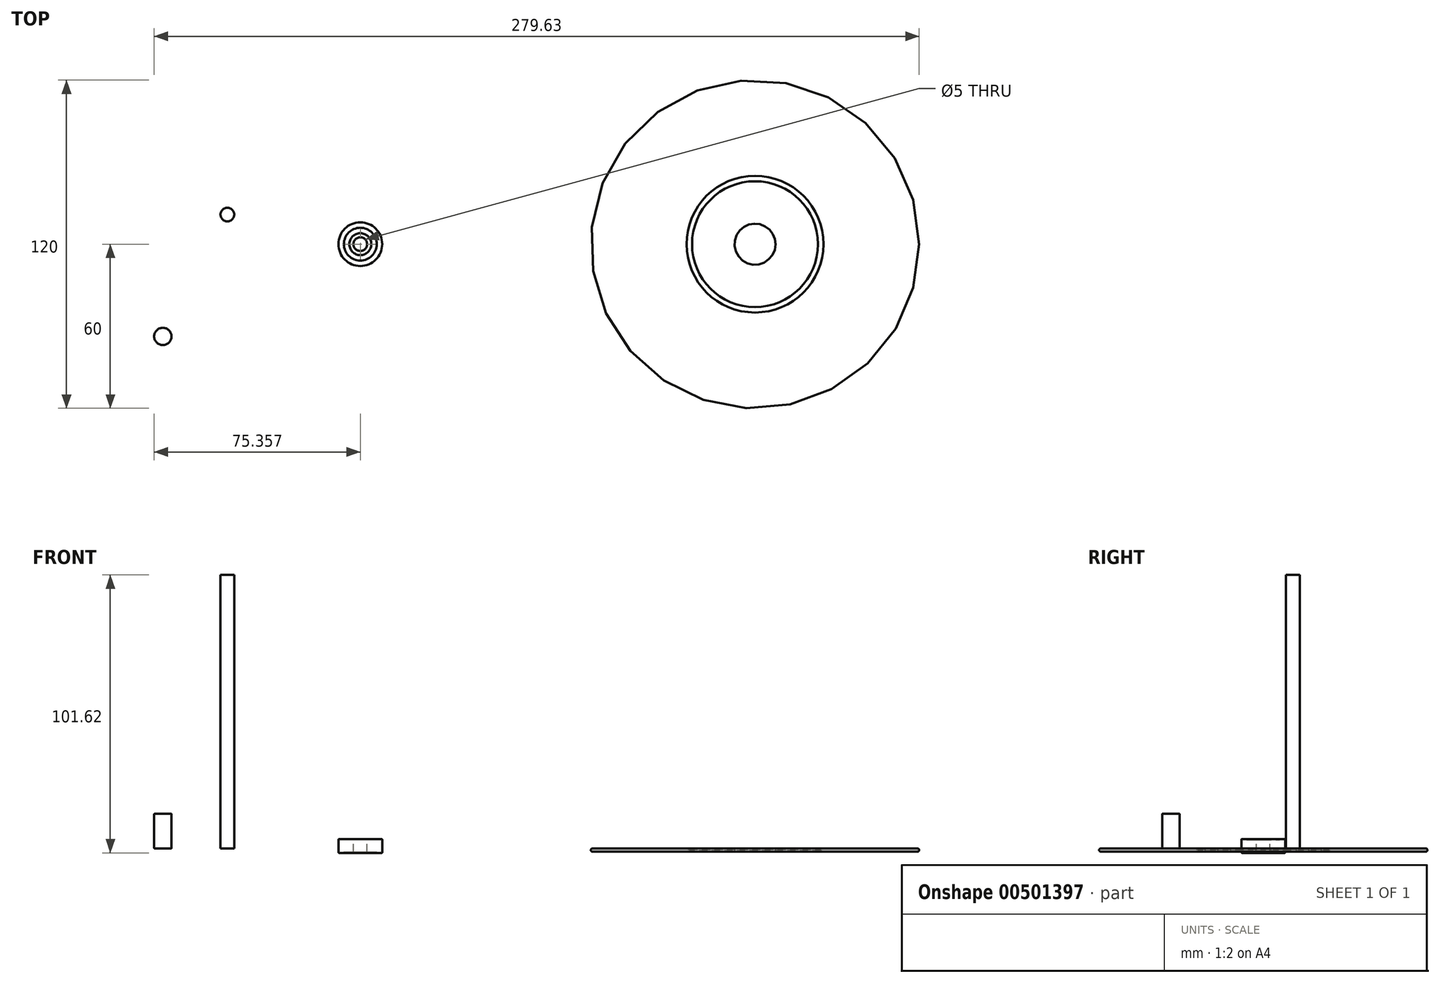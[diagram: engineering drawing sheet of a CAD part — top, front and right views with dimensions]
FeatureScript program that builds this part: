
annotation { "Feature Type Name" : "Feature", "Feature Type Description" : "" }
export const myFeature = defineFeature(function(context is Context, id is Id, definition is map)
    precondition{}
    {
        {
            var Q0;
            Q0=qCreatedBy(makeId("Front.planeOp"),FACE);
            var sketch = newSketch(context, id + "F0", { "sketchPlane" : qUnion([Q0])});
            skLineSegment(sketch, "E0", {"start": v(16.4, 3.48) * mm, "end": v(16.4, -1.62) * mm});
            skLineSegment(sketch, "E1", {"start": v(19.1, -1.62) * mm, "end": v(20.2, -1.62) * mm});
            skLineSegment(sketch, "E2", {"start": v(24.4, -1.42) * mm, "end": v(24.4, 3.18) * mm});
            skLineSegment(sketch, "E3", {"start": v(24.2, 3.38) * mm, "end": v(22.6, 3.38) * mm});
            skLineSegment(sketch, "E4", {"start": v(22.4, 3.18) * mm, "end": v(22.4, -1.42) * mm});
            skLineSegment(sketch, "E5", {"start": v(22.2, 3.38) * mm, "end": v(20.6, 3.38) * mm});
            skLineSegment(sketch, "E6", {"start": v(20.4, 3.18) * mm, "end": v(20.4, -1.42) * mm});
            skLineSegment(sketch, "E7", {"start": v(20.2, 3.38) * mm, "end": v(19.1, 3.38) * mm});
            skPoint(sketch, "E8.orphan", {"position": v(16.4, -1.62) * mm});
            skPoint(sketch, "E9.visualSharp", {"position": v(24.4, 3.38) * mm});
            skArc(sketch, "E9.filletArc", {"start": v(24.4, 3.18) * mm, "mid": v(24.35, 3.32) * mm, "end": v(24.2, 3.38) * mm});
            skPoint(sketch, "E10.visualSharp", {"position": v(24.4, -1.62) * mm});
            skArc(sketch, "E10.filletArc", {"start": v(24.2, -1.62) * mm, "mid": v(24.35, -1.56) * mm, "end": v(24.4, -1.42) * mm});
            skPoint(sketch, "E11.startSnap0", {"position": v(22.32, 3.18) * mm});
            skArc(sketch, "E12", {"start": v(22.4, 3.18) * mm, "mid": v(22.35, 3.32) * mm, "end": v(22.2, 3.38) * mm});
            skArc(sketch, "E13", {"start": v(22.6, 3.38) * mm, "mid": v(22.47, 3.32) * mm, "end": v(22.4, 3.18) * mm});
            skPoint(sketch, "E14.orphan", {"position": v(22.4, 3.38) * mm});
            skArc(sketch, "E15", {"start": v(20.4, 3.18) * mm, "mid": v(20.47, 3.32) * mm, "end": v(20.6, 3.38) * mm});
            skArc(sketch, "E16", {"start": v(20.2, 3.38) * mm, "mid": v(20.35, 3.32) * mm, "end": v(20.4, 3.18) * mm});
            skPoint(sketch, "E17.orphan", {"position": v(21.22, 3.18) * mm});
            skPoint(sketch, "E18.start.orphan", {"position": v(23.41, 3.18) * mm});
            skPoint(sketch, "E19.visualSharp", {"position": v(18.4, -1.62) * mm});
            skArc(sketch, "E20", {"start": v(20.2, -1.62) * mm, "mid": v(20.35, -1.56) * mm, "end": v(20.4, -1.42) * mm});
            skArc(sketch, "E21", {"start": v(20.4, -1.42) * mm, "mid": v(20.47, -1.56) * mm, "end": v(20.6, -1.62) * mm});
            skArc(sketch, "E22", {"start": v(22.2, -1.62) * mm, "mid": v(22.35, -1.56) * mm, "end": v(22.4, -1.42) * mm});
            skArc(sketch, "E23", {"start": v(22.4, -1.42) * mm, "mid": v(22.47, -1.56) * mm, "end": v(22.6, -1.62) * mm});
            skLineSegment(sketch, "E24.trimOffspring", {"start": v(22.6, -1.62) * mm, "end": v(24.2, -1.62) * mm});
            skLineSegment(sketch, "E25.trimOffspring", {"start": v(20.6, -1.62) * mm, "end": v(22.2, -1.62) * mm});
            skPoint(sketch, "E26.orphan", {"position": v(20.4, -1.62) * mm});
            skLineSegment(sketch, "E27", {"start": v(18.9, 2.77) * mm, "end": v(18.9, 3.18) * mm});
            skLineSegment(sketch, "E28", {"start": v(18.9, 2.77) * mm, "end": v(18.9, -1.42) * mm});
            skArc(sketch, "E29", {"start": v(18.9, 3.18) * mm, "mid": v(18.97, 3.32) * mm, "end": v(19.1, 3.38) * mm});
            skPoint(sketch, "E30.endSnap0", {"position": v(19.4, -1.62) * mm});
            skArc(sketch, "E31", {"start": v(18.9, -1.42) * mm, "mid": v(18.97, -1.56) * mm, "end": v(19.1, -1.62) * mm});
            skPoint(sketch, "E32.start.orphan", {"position": v(16.4, 2.77) * mm});
            skPoint(sketch, "E33.orphan", {"position": v(18.4, 3.18) * mm});
            skPoint(sketch, "E34.start.orphan", {"position": v(18.6, 3.18) * mm});
            skPoint(sketch, "E19.filletArc.end.orphan", {"position": v(18.6, -1.62) * mm});
            skSolve(sketch);
        }
        {
            var Q0;
            Q0=makeQuery(id+"F0.imprint","IMPRINT",FACE,{"disambiguationData":[TD([[makeQuery(id+"F0.imprint","IMPRINT",EDGE,{"derivedFrom":sQuery(id+"F0.wireOp",EDGE,"E1")}),1.0]])]});
            var Q1;
            Q1=sQuery(id+"F0.wireOp",EDGE,"E0");
            revolve(context, id + "F1", {"entities" : qUnion([Q0]), "axis" : qUnion([Q1]), "revolveType" : RevolveType.FULL});
        }
        {
            var Q0;
            Q0=makeQuery(id+"F0.imprint","IMPRINT",FACE,{"disambiguationData":[TD([[makeQuery(id+"F0.imprint","IMPRINT",EDGE,{"derivedFrom":sQuery(id+"F0.wireOp",EDGE,"E4")}),-1.0]])]});
            var Q1;
            Q1=sQuery(id+"F0.wireOp",EDGE,"E0");
            revolve(context, id + "F2", {"operationType" : NewBodyOperationType.ADD, "entities" : qUnion([Q0]), "axis" : qUnion([Q1]), "revolveType" : RevolveType.FULL});
        }
        {
            var Q0;
            Q0=makeQuery(id+"F0.imprint","IMPRINT",FACE,{"disambiguationData":[TD([[makeQuery(id+"F0.imprint","IMPRINT",EDGE,{"derivedFrom":sQuery(id+"F0.wireOp",EDGE,"E2")}),1.0]])]});
            var Q1;
            Q1=sQuery(id+"F0.wireOp",EDGE,"E0");
            revolve(context, id + "F3", {"operationType" : NewBodyOperationType.ADD, "entities" : qUnion([Q0]), "axis" : qUnion([Q1]), "revolveType" : RevolveType.FULL});
        }
        {
            var Q0;
            Q0=qCreatedBy(makeId("Top.planeOp"),FACE);
            var sketch = newSketch(context, id + "F4", { "sketchPlane" : qUnion([Q0])});
            skCircle(sketch, "E35", {"center": v(-32.2, 10.82) * mm, "radius": 2.5 * mm});
            skSolve(sketch);
        }
        {
            var Q0;
            Q0=makeQuery(id+"F4.imprint","IMPRINT",FACE,{"disambiguationData":[TD([[makeQuery(id+"F4.imprint","IMPRINT",EDGE,{"derivedFrom":sQuery(id+"F4.wireOp",EDGE,"E35")}),1.0]])]});
            extrude(context, id + "F5", {"entities" : qUnion([Q0]), "depth" : 100 * mm});
        }
        {
            var Q0;
            Q0=qCreatedBy(makeId("Top.planeOp"),FACE);
            var sketch = newSketch(context, id + "F6", { "sketchPlane" : qUnion([Q0])});
            skCircle(sketch, "E36", {"center": v(-55.77, -33.75) * mm, "radius": 3.17 * mm});
            skSolve(sketch);
        }
        {
            var Q0;
            Q0=makeQuery(id+"F6.imprint","IMPRINT",FACE,{"disambiguationData":[TD([[makeQuery(id+"F6.imprint","IMPRINT",EDGE,{"derivedFrom":sQuery(id+"F6.wireOp",EDGE,"E36")}),1.0]])]});
            extrude(context, id + "F7", {"entities" : qUnion([Q0]), "depth" : 12.7 * mm});
        }
        {
            var Q0;
            Q0=makeQuery(id+"F7.opExtrude","CAP_EDGE",EDGE,{"disambiguationData":[OSD([sQuery(id+"F6.wireOp",EDGE,"E36")])],"isStart":false});
            fillet(context, id + "F8", {"entities" : qUnion([Q0]), "radius" : 0.2 * mm, "tangentPropagation" : true, "allowEdgeOverflow" : false});
        }
        {
            var Q0;
            Q0=makeQuery(id+"F7.opExtrude","CAP_EDGE",EDGE,{"disambiguationData":[OSD([sQuery(id+"F6.wireOp",EDGE,"E36")])],"isStart":true});
            fillet(context, id + "F9", {"entities" : qUnion([Q0]), "radius" : 0.2 * mm, "tangentPropagation" : true, "allowEdgeOverflow" : false});
        }
        {
            var Q0;
            Q0=qCreatedBy(makeId("Front.planeOp"),FACE);
            var sketch = newSketch(context, id + "F10", { "sketchPlane" : qUnion([Q0])});
            skLineSegment(sketch, "E37.bottom", {"start": v(101.28, 0) * mm, "end": v(135.68, 0) * mm});
            skLineSegment(sketch, "E37.top", {"start": v(101.28, -1.2) * mm, "end": v(135.68, -1.2) * mm});
            skLineSegment(sketch, "E37.left", {"start": v(100.68, -0.6) * mm, "end": v(100.68, -0.6) * mm});
            skLineSegment(sketch, "E37.right", {"start": v(160.68, 0) * mm, "end": v(160.68, -1.2) * mm});
            skLineSegment(sketch, "E38", {"start": v(153.18, -0.6) * mm, "end": v(153.18, -0.6) * mm});
            skLineSegment(sketch, "E39", {"start": v(101.28, 0) * mm, "end": v(102.18, 0) * mm});
            skPoint(sketch, "E40.visualSharp", {"position": v(100.68, 0) * mm});
            skArc(sketch, "E40.filletArc", {"start": v(101.28, 0) * mm, "mid": v(100.86, -0.18) * mm, "end": v(100.68, -0.6) * mm});
            skPoint(sketch, "E41.visualSharp", {"position": v(100.68, -1.2) * mm});
            skArc(sketch, "E41.filletArc", {"start": v(100.68, -0.6) * mm, "mid": v(100.86, -1.02) * mm, "end": v(101.28, -1.2) * mm});
            skLineSegment(sketch, "E42", {"start": v(152.58, -1.2) * mm, "end": v(137.68, -1.2) * mm});
            skFitSpline(sketch, "E43", {"points": [v(135.68, -1.2) * mm, v(136.68, -0.9) * mm, v(137.68, -1.2) * mm], "startDerivative": vector(2, 0.9) * mm, "endDerivative": vector(2, -0.9) * mm});
            skFitSpline(sketch, "E44", {"points": [v(135.68, 0) * mm, v(136.68, -0.3) * mm, v(137.68, 0) * mm], "startDerivative": vector(2, -0.9) * mm, "endDerivative": vector(2, 0.9) * mm});
            skPoint(sketch, "E45.1.internal.orphan", {"position": v(136.68, -0.6) * mm});
            skPoint(sketch, "E46.end.orphan", {"position": v(136.68, -1.2) * mm});
            skLineSegment(sketch, "E47.trimOffspring", {"start": v(137.68, -1.2) * mm, "end": v(152.58, -1.2) * mm});
            skPoint(sketch, "E48.start.orphan", {"position": v(136.68, 0) * mm});
            skLineSegment(sketch, "E49.trimOffspring", {"start": v(137.68, 0) * mm, "end": v(152.58, 0) * mm});
            skPoint(sketch, "E50.visualSharp", {"position": v(153.18, 0) * mm});
            skArc(sketch, "E50.filletArc", {"start": v(153.18, -0.6) * mm, "mid": v(153, -0.18) * mm, "end": v(152.58, 0) * mm});
            skPoint(sketch, "E51.visualSharp", {"position": v(153.18, -1.2) * mm});
            skArc(sketch, "E51.filletArc", {"start": v(152.58, -1.2) * mm, "mid": v(153, -1.02) * mm, "end": v(153.18, -0.6) * mm});
            skSolve(sketch);
        }
        {
            var Q0;
            Q0=makeQuery(id+"F10.imprint","IMPRINT",FACE,{"disambiguationData":[TD([[makeQuery(id+"F10.imprint","IMPRINT",EDGE,{"derivedFrom":sQuery(id+"F10.wireOp",EDGE,"E37.bottom")}),-1.0]])]});
            var Q1;
            Q1=sQuery(id+"F10.wireOp",EDGE,"E37.right");
            revolve(context, id + "F11", {"entities" : qUnion([Q0]), "axis" : qUnion([Q1]), "revolveType" : RevolveType.FULL});
        }
    });
